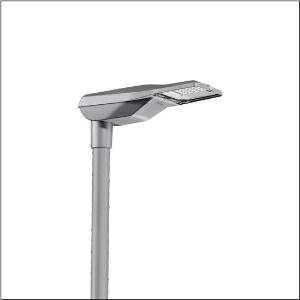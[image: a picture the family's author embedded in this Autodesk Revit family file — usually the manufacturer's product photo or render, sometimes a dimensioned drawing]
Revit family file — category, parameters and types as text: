
# Revit family: streetlight_sl_21_iq_micro___st0_8a_5xe1c21g08cb_23b1
name_source: partatom
category: Lighting Fixtures
units: mm (PartAtom-declared; Revit-internal decimal feet)

## family parameters
Cut with Voids When Loaded = No
Host = Face
Light Source = No
Part Type = Normal
Room Calculation Point = No
Round Connector Dimension = Use Diameter
Shared = No

## types (1)
- --- (1 x LED, 2380 lm, 19.4 W, 2200K)
    Apparent Load = 19 VA
    CIE Flux Codes = 38 75 97 100 100
    Color Rendering = 70
    Color Temperature = 2200K
    Default Elevation = 1800 mm
    Description = Streetlight SL 21 iQ micro, mast luminaire, primary light control with lens, of PMMA, primary optical cover: cover, of toughened safety glass, transparent, light distribution: ST0.8a, light emission: direct distribution, primary light characteristic: asymmetric, installation type: post-top, side-entry, LED, High Power LED, rated luminous flux: 2.380lm, luminous efficacy: 123lm/W, light colour: 722, colour temperature: 2200K, control: Street-Remote, Auto-Match, Temp-Guard, Lumen-Switch, Night-Set, Smart-Wire, Light-Fading, Desk-Remote (wireless, voltage-free reading and setting of iQ features in the workshop via application-optimized NFC function/RFID function), optimised constant luminous flux control (CLO 2.0), presetting dimming linear, mains connection: 220..240V, AC, 50/60Hz, start of lifetime: 19W, end of service life: 20W, reduction: 10W, luminaire housing, of diecast aluminium, powder-coated, Siteco® metallic grey (DB 702S), corrosivity category C5 mid according to DIN EN ISO 12944, please order mast flange separately, inclination adjustable: 0°, 5°, 10°, 15°, sealing non-destructively replaceable, multi-level sealing system, length: 528mm, width: 235mm, height: 110mm, mast flange for spigot size: 42mm (side-entry): 5XC10008XM4, 60/48mm (side-entry/post-top): 5XC10108XM2, 76/60mm (side-entry/post-top): 5XC10108XM1, protection rating (complete): IP66, insulation class (complete): insulation class II (safety insulation), certification: CE, ENEC, ENEC+, VDE, impact resistance: IK09, permissible operating ambient temperature for outdoor applications: -40..+50°C, standard-compliant lighting for roads and squares, packaging unit: 1 piece

Light Distribution: ST0.8a
    Height = 110 mm
    Lamp = 1 x LED
    Lamp Light Flux = 2380 lm
    Lamp Power = 19.4 W
    Lamp count = 1
    Length = 528 mm
    Luminous efficacy = 123 lm/W
    Manufacturer = Siteco
    ModVariant = No
    Model = 5XE1C21G08CB
    Number of Poles = 1
    OnlyDefault = Yes
    Power Factor = 1
    Product Name = Streetlight SL 21 iQ micro | ST0.8a
    Product group = mast luminaire | pylon top
    ProductGroupID = 6100
    Protection Class = Protection class II
    Protection Degree = IP 66
    RLX_Detail_Level = 1
    RLX_Emergency_Light_Flux = 0 lm
    RLX_Emergency_Type = 0
    RLX_Emergency_Type_DB = No
    RlxData = <blob elided: 99305 chars, md5=ce083a27>
    Socket = socket
    Standby Power = 0 W
    System Light Flux = 2380 lm
    System Power = 19 W
    Type Comments = factory setting: luminous flux: 100 % | dim-lin: 254 | 387 mA
    Type Image = l_1006881.jpg
    URL = http://relux.com
    VarID = @adj_069825
    Voltage = 0 V
    Weight = 0.00 kg
    Width = 235 mm

## geometry (parser evidence)
native form markers: Blend x4, Sweep x11
no freeform markers — native parametric forms only
